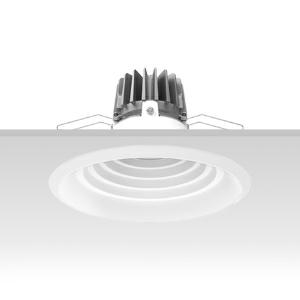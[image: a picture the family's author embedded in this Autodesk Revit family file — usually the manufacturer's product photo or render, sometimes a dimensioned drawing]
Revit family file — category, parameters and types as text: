
# Revit family: 3f_filippi_-_3f_reno_bianco_ugr_3f_filippi_-_30741_-_3f_reno_200_wh_2000-930_ep_ugr
name_source: partatom
category: Lighting Fixtures
units: mm (PartAtom-declared; Revit-internal decimal feet)

## family parameters
Cut with Voids When Loaded = No
Host = Face
Light Source = No
Part Type = Normal
Room Calculation Point = No
Round Connector Dimension = Use Diameter
Shared = No

## types (1)
- 3F Filippi - 3F Reno Bianco UGR (1 x LED, 2354 lm, 25 W, 3000 K)
    Apparent Load = 25 VA
    Approval mark = ENEC
    CIE Flux Codes = 90 100 100 100 100
    Color Rendering = 90
    Color Temperature = 3000 K
    Control Gear = Electronic ballast
    Default Elevation = 1800 mm
    Description = ILLUMINOTECHNICAL
Luminous efficiency 100% (DLOR 100%, ULOR 0%).
Initial luminous flux of the luminaire 2354 lm.
Emergency luminaire luminous flux BLF 16.7%.
Direct symmetric UGR distribution.
Installation Interdistance Transv.D = 0.99 x hu - Long.D = 1.01 x hu.
Average luminance <500 cd/m² for radial angles >65°.
Tabular UGR (CIE 117 - 4H-8H; S=0.25H; 70/50/20): RUG 17.2 - 17.2.
Beam angle: 64° - 65°.
Luminous efficacy 94 lm/W.
Lifetime (L90/B10): 30000 h. (tq+25°C)
Lifetime (L85/B10): 50000 h. (tq+25°C)
Lifetime (L70/B10): 80000 h. (tq+25°C)
Sudden decreased luminous flux after 50000 hours: 0% (C0).
Photobiological safety in compliance with IEC/TR 62778: RG0 risk exempt, (IEC 62471).
In compliance with IEC/EN 62722-2-1 - IEC/EN 62717 standards.

SOURCE
Compact LED module 2000/930.
Energy efficiency class (UE 2019/2020 - UE 2019/2015): E.
CIE 13.3 Colour rendering index: CRI >90 (R9 >50%).
IES TM-30 Fidelity Index: Rf = 92 Rg = 101.
CCT nominal colour temperature 3000 K.
Colour initial tolerance (MacAdam): SDCM 3.
Zhaga Book 3 compliant.

MECHANICAL
Passive heat dissipator in die-casting aluminium, oversized, for optimum thermal management of the LED module.
Parabolic element with graduated/concentric rings in white polycarbonate.
Internal specular metallic louvre to optimise control of the luminous flux in polycarbonate.
Transparent external lens with glossy and satin differentiated surfaces, with a cooling and anti-insect system in methacrylate (PMMA).
Fastening spring clips in stainless steel.
Dimensions: diameter 216 mm, height 142 mm. Weight 1.36 kg.
IP44 protection degree for exposed part, IP20 for recessed part.
Mechanical strength to impacts IK04 (0.5 joule).
Glow-wire test resistance 650°C.

ELECTRICAL
Wiring on a separate unit.
Halogen Free electronic wiring 230V-50/60Hz, power factor 0.90, THD <25%, constant output current, SELV, class II, 1 driver.
Power of the luminaire 25 W.
CE - IEC 60598-1 - EN 60598-1.
EP maintained emergency wiring on board, 1h duration, 24h recharge; compliant with EN 60598-2-22, excluding high risk areas.
SAFE FLICKER: PstLM=<1 and SVM=<0.4 (IEC TR 61547-1 and IEC TR 63158), to ensure a more comfortable and safe light.
Ambient temperature from +5°C to +25°C.
Temperature class T6 max 85°C.
Relative humidity UR: <85%.

INSTALLATION
Pull-up recessed fitting.
False ceiling carving: 200 mm.
All accessories dedicated to this product are available on the Catalog and on our website www.3F-Filippi.com.

APPLICATIONS
In environments with VDTs, managerial offices and staterooms, public offices and schools.
In false ceilings with narrow voids.

WARNING
Luminaire designed for disposal/recycling at end-of-life.
Replaceable (LED only) light source by a professional. Replaceable control gear by a professional.
    Height = 0 mm  [stored 0 ft]
    Lamp = 1 x LED
    Lamp Light Flux = 2354 lm
    Lamp Power = 25 W
    Lamp count = 1
    Length = 216 mm
    Lifetime = 50000 h
    Luminous efficacy = 94 lm/W
    Manufacturer = 3F Filippi
    ModVariant = No
    Model = 3F Filippi - 30741 - 3F Reno 200 WH 2000-930 EP UGR
    Mounting Place = Ceiling
    Mounting Type = Recessed
    Number of Poles = 1
    OnlyDefault = Yes
    Power Factor = 1
    Product Name = 3F Filippi - 3F Reno Bianco UGR
    Product group = recessed luminaire
    ProductGroupID = 4
    Protection Class = Protection class II
    Protection Degree = IP 20
    RLX_Detail_Level = 1
    RLX_Emergency_Light_Flux = 0 lm
    RLX_Emergency_Type = 0
    RLX_Emergency_Type_DB = No
    RlxData = <blob elided: 88449 chars, md5=66b6a2a4>
    Socket = socket
    Standby Power = 0 W
    System Light Flux = 2354 lm
    System Power = 25 W
    Type Comments = Product without accessories
    Type Image = 3ffilippi_3f_reno_200_wh_2000.jpg
    URL = http://relux.com
    VarID = ---
    Voltage = 0 V
    Weight = 0.00 kg
    Width = 0 mm  [stored 0 ft]

note: [stored X ft] marks values corroborated as IEEE doubles in the binary element streams (Revit-internal decimal feet)

## geometry (parser evidence)
native form markers: Blend x4, Sweep x11
no freeform markers — native parametric forms only
